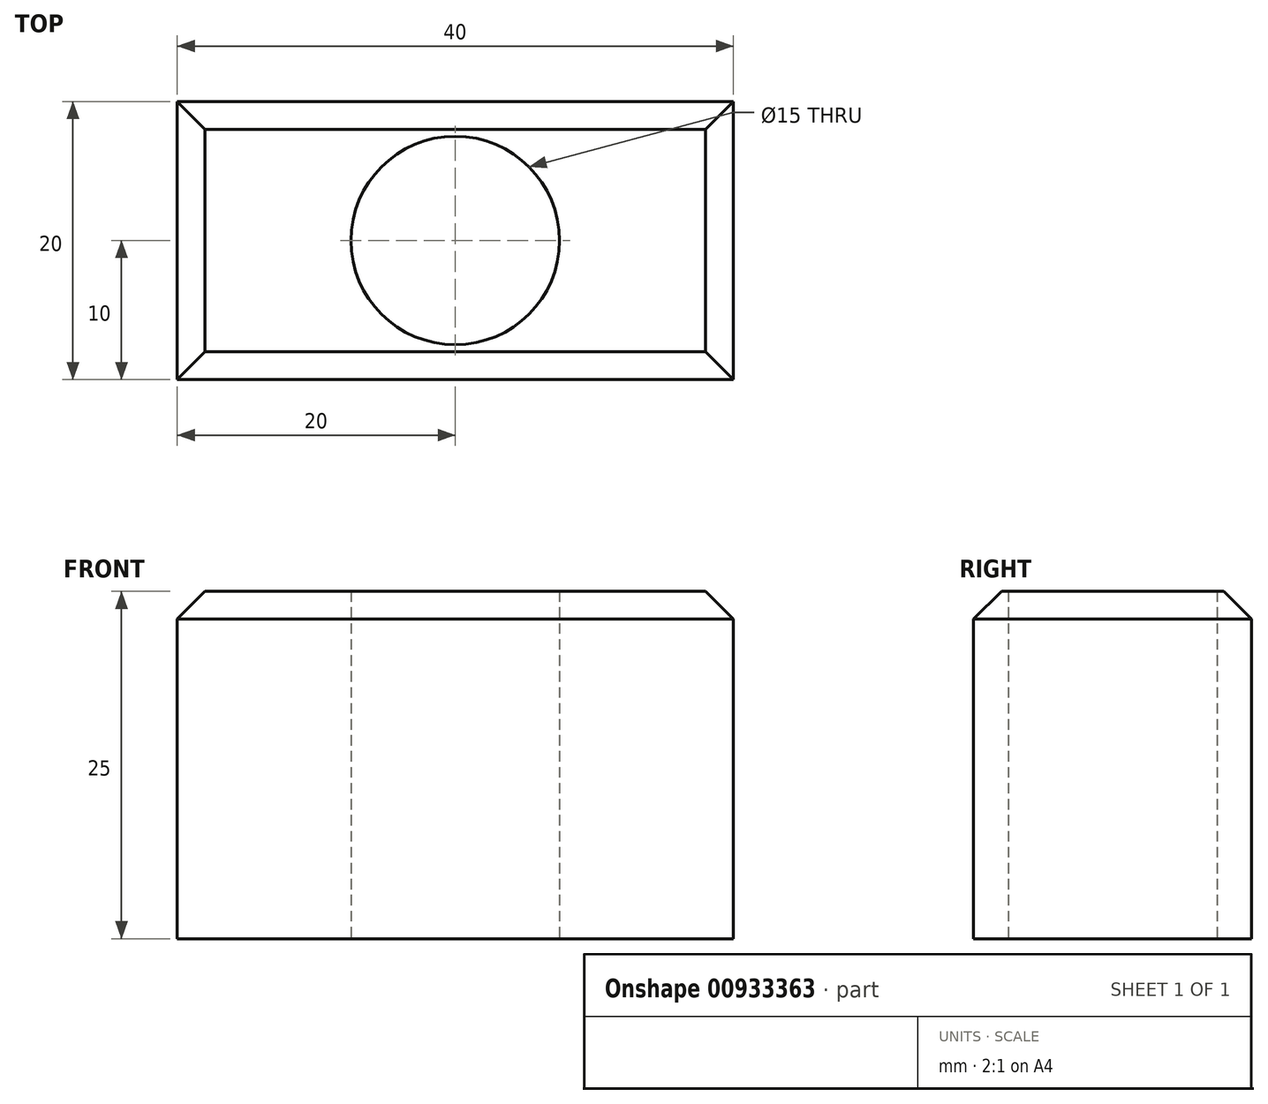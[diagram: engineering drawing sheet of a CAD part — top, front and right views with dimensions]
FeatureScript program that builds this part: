
annotation { "Feature Type Name" : "Feature", "Feature Type Description" : "" }
export const myFeature = defineFeature(function(context is Context, id is Id, definition is map)
    precondition{}
    {
        {
            var Q0;
            Q0=qCreatedBy(makeId("Top.planeOp"),FACE);
            var sketch = newSketch(context, id + "F0", { "sketchPlane" : qUnion([Q0])});
            skLineSegment(sketch, "E0", {"start": v(0, 0) * mm, "end": v(0, 20) * mm});
            skLineSegment(sketch, "E1", {"start": v(0, 20) * mm, "end": v(40, 20) * mm});
            skLineSegment(sketch, "E2", {"start": v(40, 20) * mm, "end": v(40, 0) * mm});
            skLineSegment(sketch, "E3", {"start": v(40, 0) * mm, "end": v(0, 0) * mm});
            skLineSegment(sketch, "E4", {"start": v(0, 10) * mm, "end": v(40, 10) * mm, "construction": true});
            skCircle(sketch, "E5", {"center": v(20, 10) * mm, "radius": 7.5 * mm});
            skSolve(sketch);
        }
        {
            var Q0;
            Q0=makeQuery(id+"F0.imprint","IMPRINT",FACE,{"disambiguationData":[TD([[makeQuery(id+"F0.imprint","IMPRINT",EDGE,{"derivedFrom":sQuery(id+"F0.wireOp",EDGE,"E0")}),-1.0]])]});
            extrude(context, id + "F1", {"entities" : qUnion([Q0]), "depth" : 25 * mm, "offsetDistance" : 25 * mm});
        }
        {
            var Q0;
            Q0=makeQuery(id+"F1.opExtrude","CAP_EDGE",EDGE,{"disambiguationData":[OSD([sQuery(id+"F0.wireOp",EDGE,"E3")])],"isStart":false});
            var Q1;
            Q1=makeQuery(id+"F1.opExtrude","CAP_EDGE",EDGE,{"disambiguationData":[OSD([sQuery(id+"F0.wireOp",EDGE,"E0")])],"isStart":false});
            var Q2;
            Q2=makeQuery(id+"F1.opExtrude","CAP_EDGE",EDGE,{"disambiguationData":[OSD([sQuery(id+"F0.wireOp",EDGE,"E1")])],"isStart":false});
            var Q3;
            Q3=makeQuery(id+"F1.opExtrude","CAP_EDGE",EDGE,{"disambiguationData":[OSD([sQuery(id+"F0.wireOp",EDGE,"E2")])],"isStart":false});
            chamfer(context, id + "F2", {"entities" : qUnion([Q0, Q1, Q2, Q3]), "width" : 2 * mm, "tangentPropagation" : true});
        }
    });
